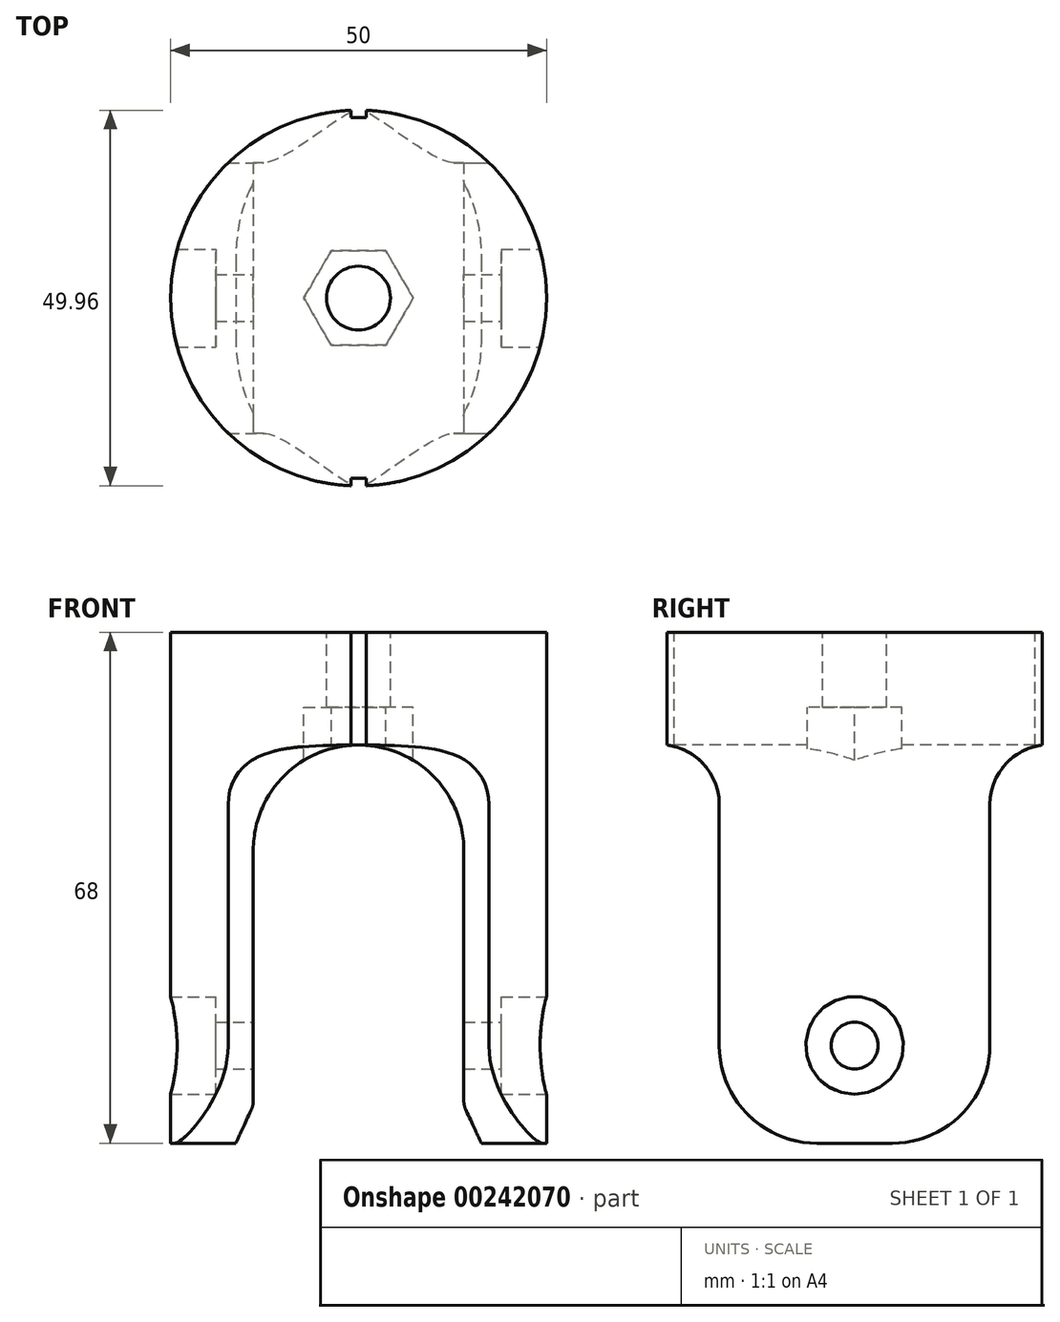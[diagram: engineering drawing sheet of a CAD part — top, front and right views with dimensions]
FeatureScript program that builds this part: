
annotation { "Feature Type Name" : "Feature", "Feature Type Description" : "" }
export const myFeature = defineFeature(function(context is Context, id is Id, definition is map)
    precondition{}
    {
        {
            var Q0;
            Q0=qCreatedBy(makeId("Top.planeOp"),FACE);
            var sketch = newSketch(context, id + "F0", { "sketchPlane" : qUnion([Q0])});
            skCircle(sketch, "E0", {"center": v(0, 0) * mm, "radius": 25 * mm});
            skSolve(sketch);
        }
        {
            var Q0;
            Q0=qSketchRegion(id+"F0",true);
            extrude(context, id + "F1", {"entities" : qUnion([Q0]), "oppositeDirection" : true, "depth" : 68 * mm});
        }
        {
            var Q0;
            Q0=qCreatedBy(makeId("Right.planeOp"),FACE);
            var sketch = newSketch(context, id + "F2", { "sketchPlane" : qUnion([Q0])});
            skCircle(sketch, "E1", {"center": v(0, -55) * mm, "radius": 40 * mm, "construction": true});
            skLineSegment(sketch, "E2", {"start": v(-28, -15) * mm, "end": v(-25, -15) * mm});
            skLineSegment(sketch, "E3", {"start": v(-18, -22.94) * mm, "end": v(-18, -55) * mm});
            skLineSegment(sketch, "E4", {"start": v(-28, -15) * mm, "end": v(-28, -73) * mm});
            skLineSegment(sketch, "E5", {"start": v(-28, -73) * mm, "end": v(0, -73) * mm});
            skLineSegment(sketch, "E6", {"start": v(0, -68) * mm, "end": v(-5, -68) * mm});
            skArc(sketch, "E7", {"start": v(-18, -55) * mm, "mid": v(-14.2, -64.2) * mm, "end": v(-5, -68) * mm});
            skLineSegment(sketch, "E8", {"start": v(0, 0) * mm, "end": v(0, -95) * mm, "construction": true});
            skArc(sketch, "E9", {"start": v(-18, -22.94) * mm, "mid": v(-20, -17.65) * mm, "end": v(-25, -15) * mm});
            skLineSegment(sketch, "E10.MirrorCS", {"start": v(28, -15) * mm, "end": v(25, -15) * mm});
            skArc(sketch, "E11.MirrorCS", {"start": v(18, -22.94) * mm, "mid": v(20, -17.65) * mm, "end": v(25, -15) * mm});
            skArc(sketch, "E12.MirrorCS", {"start": v(18, -55) * mm, "mid": v(14.2, -64.2) * mm, "end": v(5, -68) * mm});
            skLineSegment(sketch, "E13.MirrorCS", {"start": v(0, -68) * mm, "end": v(5, -68) * mm});
            skLineSegment(sketch, "E14.MirrorCS", {"start": v(18, -22.94) * mm, "end": v(18, -55) * mm});
            skLineSegment(sketch, "E15.MirrorCS", {"start": v(28, -73) * mm, "end": v(0, -73) * mm});
            skLineSegment(sketch, "E16.MirrorCS", {"start": v(28, -15) * mm, "end": v(28, -73) * mm});
            skSolve(sketch);
        }
        {
            var Q0;
            Q0=qSketchRegion(id+"F2",true);
            extrude(context, id + "F3", {"entities" : qUnion([Q0]), "operationType" : NewBodyOperationType.REMOVE, "endBound" : BoundingType.THROUGH_ALL, "oppositeDirection" : true, "depth" : 25 * mm, "hasSecondDirection" : true, "secondDirectionBound" : SecondDirectionBoundingType.THROUGH_ALL, "secondDirectionOppositeDirection" : false, "secondDirectionDepth" : 25 * mm});
        }
        {
            var Q0;
            Q0=qCreatedBy(makeId("Front.planeOp"),FACE);
            var sketch = newSketch(context, id + "F4", { "sketchPlane" : qUnion([Q0])});
            skArc(sketch, "E17", {"start": v(14, -29) * mm, "mid": v(0, -15) * mm, "end": v(-14, -29) * mm});
            skLineSegment(sketch, "E18", {"start": v(-14, -29) * mm, "end": v(-14, -62.33) * mm});
            skLineSegment(sketch, "E19", {"start": v(14, -29) * mm, "end": v(14, -62.33) * mm});
            skLineSegment(sketch, "E20", {"start": v(16.33, -68) * mm, "end": v(-16.33, -68) * mm});
            skLineSegment(sketch, "E21", {"start": v(-14.28, -63.6) * mm, "end": v(-16.33, -68) * mm});
            skLineSegment(sketch, "E22", {"start": v(14.28, -63.6) * mm, "end": v(16.33, -68) * mm});
            skLineSegment(sketch, "E23", {"start": v(-14, -63) * mm, "end": v(14, -63) * mm, "construction": true});
            skPoint(sketch, "E24.visualSharp", {"position": v(-14, -63) * mm});
            skArc(sketch, "E24.filletArc", {"start": v(-14.28, -63.6) * mm, "mid": v(-14.07, -62.98) * mm, "end": v(-14, -62.33) * mm});
            skPoint(sketch, "E25.visualSharp", {"position": v(14, -63) * mm});
            skArc(sketch, "E25.filletArc", {"start": v(14, -62.33) * mm, "mid": v(14.07, -62.98) * mm, "end": v(14.28, -63.6) * mm});
            skSolve(sketch);
        }
        {
            var Q0;
            Q0=qSketchRegion(id+"F4",true);
            extrude(context, id + "F5", {"entities" : qUnion([Q0]), "operationType" : NewBodyOperationType.REMOVE, "endBound" : BoundingType.THROUGH_ALL, "oppositeDirection" : true, "depth" : 25 * mm, "hasSecondDirection" : true, "secondDirectionBound" : SecondDirectionBoundingType.THROUGH_ALL, "secondDirectionOppositeDirection" : false, "secondDirectionDepth" : 25 * mm});
        }
        {
            var Q0;
            Q0=qCreatedBy(makeId("Front.planeOp"),FACE);
            var sketch = newSketch(context, id + "F6", { "sketchPlane" : qUnion([Q0])});
            skLineSegment(sketch, "E26", {"start": v(-30.91, -55) * mm, "end": v(31.05, -55) * mm, "construction": true});
            skLineSegment(sketch, "E27", {"start": v(-26, -48.5) * mm, "end": v(-19, -48.5) * mm});
            skLineSegment(sketch, "E28", {"start": v(-19, -48.5) * mm, "end": v(-19, -51.88) * mm});
            skLineSegment(sketch, "E29", {"start": v(-19, -51.88) * mm, "end": v(0, -51.88) * mm});
            skLineSegment(sketch, "E30", {"start": v(-26, -48.5) * mm, "end": v(-26, -55) * mm});
            skLineSegment(sketch, "E31", {"start": v(-26, -55) * mm, "end": v(0, -55) * mm});
            skLineSegment(sketch, "E32.MirrorCS", {"start": v(26, -48.5) * mm, "end": v(19, -48.5) * mm});
            skLineSegment(sketch, "E33.MirrorCS", {"start": v(19, -48.5) * mm, "end": v(19, -51.88) * mm});
            skLineSegment(sketch, "E34.MirrorCS", {"start": v(19, -51.88) * mm, "end": v(0, -51.88) * mm});
            skLineSegment(sketch, "E35.MirrorCS", {"start": v(26, -48.5) * mm, "end": v(26, -55) * mm});
            skLineSegment(sketch, "E36.MirrorCS", {"start": v(26, -55) * mm, "end": v(0, -55) * mm});
            skSolve(sketch);
        }
        {
            var Q0;
            Q0=qSketchRegion(id+"F6",true);
            var Q1;
            Q1=sQuery(id+"F6.wireOp",EDGE,"E26");
            revolve(context, id + "F7", {"operationType" : NewBodyOperationType.REMOVE, "entities" : qUnion([Q0]), "axis" : qUnion([Q1]), "revolveType" : RevolveType.FULL, "oppositeDirection" : true});
        }
        {
            var Q0;
            Q0=makeQuery(id+"F1.opExtrude","CAP_FACE",FACE,{"disambiguationData":[OSD([sQuery(id+"F0.wireOp",EDGE,"E0")])],"isStart":true});
            var sketch = newSketch(context, id + "F8", { "sketchPlane" : qUnion([Q0])});
            skCircle(sketch, "E37", {"center": v(0, 0) * mm, "radius": 4.25 * mm});
            skSolve(sketch);
        }
        {
            var Q0;
            Q0=qSketchRegion(id+"F8",true);
            extrude(context, id + "F9", {"entities" : qUnion([Q0]), "operationType" : NewBodyOperationType.REMOVE, "oppositeDirection" : true, "depth" : 25 * mm});
        }
        {
            var Q0;
            Q0=qCreatedBy(makeId("Top.planeOp"),FACE);
            cPlane(context, id + "F10", {"entities" : qUnion([Q0]), "cplaneType" : CPlaneType.OFFSET, "offset" : 10 * mm, "oppositeDirection" : true, "width" : 150 * mm, "height" : 150 * mm});
        }
        {
            var Q0;
            Q0=qCreatedBy(id+"F10.planeOp",FACE);
            var sketch = newSketch(context, id + "F11", { "sketchPlane" : qUnion([Q0])});
            skCircle(sketch, "E38.cCircle", {"center": v(0, 0) * mm, "radius": 6.3 * mm, "construction": true});
            skLineSegment(sketch, "E38.0", {"start": v(7.27, 0) * mm, "end": v(3.64, -6.3) * mm});
            skLineSegment(sketch, "E38.1", {"start": v(3.64, -6.3) * mm, "end": v(-3.64, -6.3) * mm});
            skLineSegment(sketch, "E38.2", {"start": v(-3.64, -6.3) * mm, "end": v(-7.27, 0) * mm});
            skLineSegment(sketch, "E38.3", {"start": v(-7.27, 0) * mm, "end": v(-3.64, 6.3) * mm});
            skLineSegment(sketch, "E38.4", {"start": v(-3.64, 6.3) * mm, "end": v(3.64, 6.3) * mm});
            skLineSegment(sketch, "E38.5", {"start": v(3.64, 6.3) * mm, "end": v(7.27, 0) * mm});
            skPoint(sketch, "E38.0.midPoint", {"position": v(5.46, -3.15) * mm});
            skSolve(sketch);
        }
        {
            var Q0;
            Q0=qSketchRegion(id+"F11",true);
            extrude(context, id + "F12", {"entities" : qUnion([Q0]), "operationType" : NewBodyOperationType.REMOVE, "oppositeDirection" : true, "depth" : 10 * mm});
        }
        {
            var Q0;
            Q0=makeQuery(id+"F1.opExtrude","CAP_FACE",FACE,{"disambiguationData":[OSD([sQuery(id+"F0.wireOp",EDGE,"E0")])],"isStart":true});
            var sketch = newSketch(context, id + "F13", { "sketchPlane" : qUnion([Q0])});
            skLineSegment(sketch, "E39.bottom", {"start": v(-1, 24) * mm, "end": v(1, 24) * mm});
            skLineSegment(sketch, "E39.top", {"start": v(-1, 26) * mm, "end": v(1, 26) * mm});
            skLineSegment(sketch, "E39.left", {"start": v(-1, 24) * mm, "end": v(-1, 26) * mm});
            skLineSegment(sketch, "E39.right", {"start": v(1, 24) * mm, "end": v(1, 26) * mm});
            skLineSegment(sketch, "E40.bottom", {"start": v(-1, -26) * mm, "end": v(1, -26) * mm});
            skLineSegment(sketch, "E40.top", {"start": v(-1, -24) * mm, "end": v(1, -24) * mm});
            skLineSegment(sketch, "E40.left", {"start": v(-1, -26) * mm, "end": v(-1, -24) * mm});
            skLineSegment(sketch, "E40.right", {"start": v(1, -26) * mm, "end": v(1, -24) * mm});
            skLineSegment(sketch, "E41", {"start": v(0, 18.47) * mm, "end": v(0, -17.11) * mm, "construction": true});
            skPoint(sketch, "E42", {"position": v(0, 24) * mm});
            skPoint(sketch, "E43", {"position": v(0, -24) * mm});
            skSolve(sketch);
        }
        {
            var Q0;
            Q0=qSketchRegion(id+"F13",true);
            extrude(context, id + "F14", {"entities" : qUnion([Q0]), "operationType" : NewBodyOperationType.REMOVE, "oppositeDirection" : true, "depth" : 25 * mm});
        }
    });
